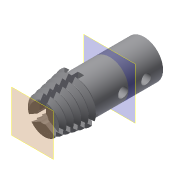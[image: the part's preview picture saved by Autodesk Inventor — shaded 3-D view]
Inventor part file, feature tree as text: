
AUTODESK INVENTOR PART (.ipt)
format: ipt  version: 2019.4 (Build 234330000, 330)  size: 741,376 bytes
history: native  units: mm
features: sketch x9, extrude x6, projected_geometry x4, plane x3, reference x3, other x3, sweep x1, revolve x1, pattern_circular x1, chamfer x1
ambient origin geometry x8: Origin, YZ Plane, XZ Plane, XY Plane, X Axis, Y Axis, Z Axis, Center Point
bodies: Solid1 (feature_tree)
feature tree (32):
  plane  "Work Plane1"
  extrude  "Extrusion1"  Depth=2.2mm
  plane  "Work Plane2"
  sweep  "Sweep1"
  plane  "Work Plane3"
  extrude  "Extrusion2"  Depth=1.79mm
  revolve  "Revolution2"  [1 undecoded]
  extrude  "Extrusion4"  Depth=3.0mm TaperAngle=0.0deg
  pattern_circular  "Circular Pattern2"  [2 undecoded]
  extrude  "Extrusion5"  TaperAngle=90.0deg  [1 undecoded]
  chamfer  "Chamfer1"  Distance=11.0mm
  extrude  "Extrusion6"  Depth=30.0mm TaperAngle=360.0deg
  extrude  "Extrusion7"  Depth=0.1mm
  sketch  "Sketch1"  dims[d0=5.1mm d1=2.2mm]
  reference  "Reference1"
  sketch  "3D Sketch1"
  other  "Helical Curve1"
  sketch  "Sketch4"  dims[d2=20.0mm d3=0.0mm d4=2.2mm]
  reference  "Reference2"
  sketch  "Sketch5"  dims[d13=11.0mm]
  reference  "Reference3"
  sketch  "Sketch7"  dims[d15=1.8mm d16=0.0mm d17=11.0mm d18=1.8mm d19=60.0mm d20=7.0mm d24=1.79mm]
  projected_geometry  "Projected Loop2"
  projected_geometry  "Projected Loop3"
  sketch  "Sketch8"  dims[d25=0.9mm d26=0.0mm d27=0.0mm]
  sketch  "Sketch9"  dims[d28=12.25mm d29=3.0mm d30=0.0mm]
  projected_geometry  "Projected Loop4"
  sketch  "Sketch10"  dims[d37=1.6mm]
  projected_geometry  "Projected Loop5"
  sketch  "Sketch11"  dims[d38=1.45mm d39=2.55mm d40=90.0deg d41=11.0mm d42=0.0mm d43=30.0mm d44=360.0deg d46=0.1mm d47=20.0mm d48=0.0mm d49=1.0mm d50=2.0mm d51=45.0deg d52=2.8mm d53=2.8mm d54=20.0mm d55=0.0mm d56=7.0mm d57=0.0mm]
  other  "Assembly2"
  other  "00_coupler_5_3:1"
note: 4 required parameter values undecoded (feature->parameter linkage not recoverable at this tier; creation-order binding heuristic only, values carry confidence <= 0.55)